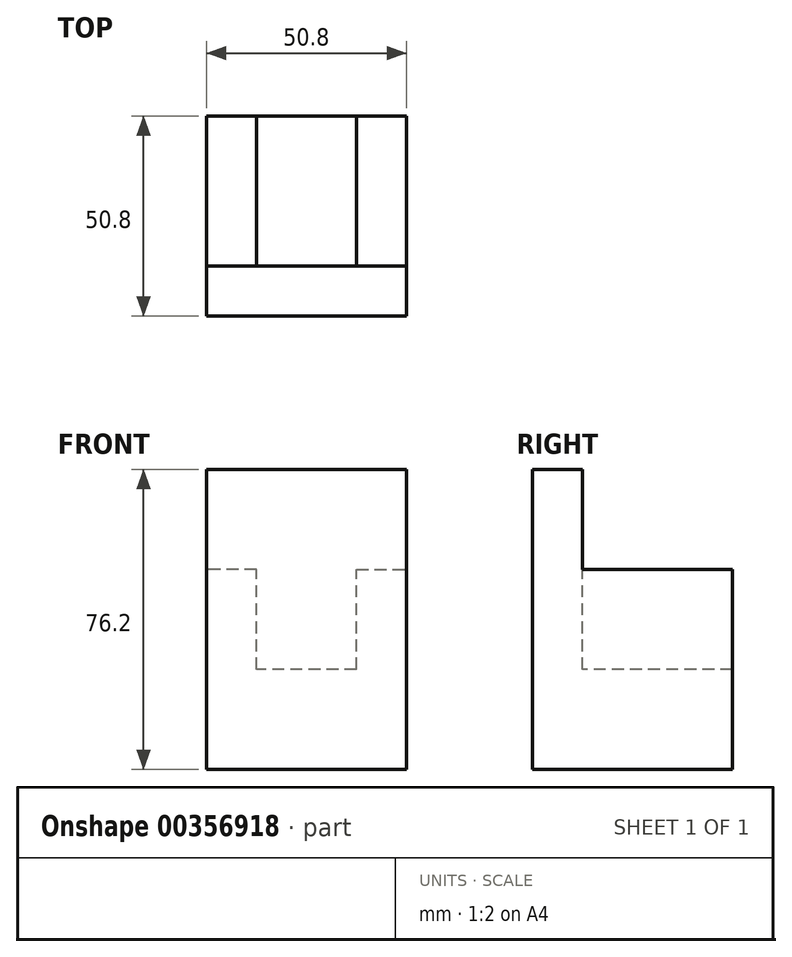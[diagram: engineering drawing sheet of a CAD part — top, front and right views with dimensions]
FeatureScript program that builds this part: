
annotation { "Feature Type Name" : "Feature", "Feature Type Description" : "" }
export const myFeature = defineFeature(function(context is Context, id is Id, definition is map)
    precondition{}
    {
        {
            var Q0;
            Q0=qCreatedBy(makeId("Front.planeOp"),FACE);
            var sketch = newSketch(context, id + "F0", { "sketchPlane" : qUnion([Q0])});
            skLineSegment(sketch, "E0.bottom", {"start": v(0, 0) * mm, "end": v(-50.8, 0) * mm});
            skLineSegment(sketch, "E0.top", {"start": v(0, -76.2) * mm, "end": v(-50.8, -76.2) * mm});
            skLineSegment(sketch, "E0.left", {"start": v(0, 0) * mm, "end": v(0, -76.2) * mm});
            skLineSegment(sketch, "E0.right", {"start": v(-50.8, 0) * mm, "end": v(-50.8, -76.2) * mm});
            skSolve(sketch);
        }
        {
            var Q0;
            Q0=makeQuery(id+"F0.imprint","IMPRINT",FACE,{"disambiguationData":[TD([[makeQuery(id+"F0.imprint","IMPRINT",EDGE,{"derivedFrom":sQuery(id+"F0.wireOp",EDGE,"E0.bottom")}),1.0]])]});
            extrude(context, id + "F1", {"entities" : qUnion([Q0]), "oppositeDirection" : true, "depth" : 50.8 * mm});
        }
        {
            var Q0;
            Q0=makeQuery(id+"F1.opExtrude","SWEPT_FACE",FACE,{"disambiguationData":[OSD([sQuery(id+"F0.wireOp",EDGE,"E0.bottom")])]});
            var sketch = newSketch(context, id + "F2", { "sketchPlane" : qUnion([Q0])});
            skLineSegment(sketch, "E1.bottom", {"start": v(-12.7, 50.8) * mm, "end": v(-38.1, 50.8) * mm});
            skLineSegment(sketch, "E1.top", {"start": v(-12.7, 12.7) * mm, "end": v(-38.1, 12.7) * mm});
            skLineSegment(sketch, "E1.left", {"start": v(-12.7, 50.8) * mm, "end": v(-12.7, 12.7) * mm});
            skLineSegment(sketch, "E1.right", {"start": v(-38.1, 50.8) * mm, "end": v(-38.1, 12.7) * mm});
            skSolve(sketch);
        }
        {
            var Q0;
            Q0=makeQuery(id+"F2.imprint","IMPRINT",FACE,{"disambiguationData":[TD([[makeQuery(id+"F2.imprint","IMPRINT",EDGE,{"derivedFrom":sQuery(id+"F2.wireOp",EDGE,"E1.bottom")}),1.0]])]});
            extrude(context, id + "F3", {"entities" : qUnion([Q0]), "operationType" : NewBodyOperationType.REMOVE, "oppositeDirection" : true, "depth" : 50.8 * mm});
        }
        {
            var Q0;
            Q0=makeQuery(id+"F1.opExtrude","SWEPT_FACE",FACE,{"disambiguationData":[OSD([sQuery(id+"F0.wireOp",EDGE,"E0.right")])]});
            var sketch = newSketch(context, id + "F4", { "sketchPlane" : qUnion([Q0])});
            skLineSegment(sketch, "E2.bottom", {"start": v(-50.8, 0) * mm, "end": v(-12.7, 0) * mm});
            skLineSegment(sketch, "E2.top", {"start": v(-50.8, -25.4) * mm, "end": v(-12.7, -25.4) * mm});
            skLineSegment(sketch, "E2.left", {"start": v(-50.8, 0) * mm, "end": v(-50.8, -25.4) * mm});
            skLineSegment(sketch, "E2.right", {"start": v(-12.7, 0) * mm, "end": v(-12.7, -25.4) * mm});
            skSolve(sketch);
        }
        {
            var Q0;
            Q0=makeQuery(id+"F4.imprint","IMPRINT",FACE,{"disambiguationData":[TD([[makeQuery(id+"F4.imprint","IMPRINT",EDGE,{"derivedFrom":sQuery(id+"F4.wireOp",EDGE,"E2.bottom")}),-1.0]])]});
            var Q1;
            Q1 = qSketchRegion(id + "F4", true);
            extrude(context, id + "F5", {"entities" : qUnion([Q0, Q1]), "operationType" : NewBodyOperationType.REMOVE, "oppositeDirection" : true, "depth" : 25.4 * mm});
        }
        {
            var Q0;
            Q0=makeQuery(id+"F1.opExtrude","SWEPT_FACE",FACE,{"disambiguationData":[OSD([sQuery(id+"F0.wireOp",EDGE,"E0.left")])]});
            var sketch = newSketch(context, id + "F6", { "sketchPlane" : qUnion([Q0])});
            skLineSegment(sketch, "E3.bottom", {"start": v(50.8, 0) * mm, "end": v(12.7, 0) * mm});
            skLineSegment(sketch, "E3.top", {"start": v(50.8, -25.4) * mm, "end": v(12.7, -25.4) * mm});
            skLineSegment(sketch, "E3.left", {"start": v(50.8, 0) * mm, "end": v(50.8, -25.4) * mm});
            skLineSegment(sketch, "E3.right", {"start": v(12.7, 0) * mm, "end": v(12.7, -25.4) * mm});
            skSolve(sketch);
        }
        {
            var Q0;
            Q0 = qSketchRegion(id + "F6", true);
            extrude(context, id + "F7", {"entities" : qUnion([Q0]), "operationType" : NewBodyOperationType.REMOVE, "oppositeDirection" : true, "depth" : 25.4 * mm});
        }
    });
